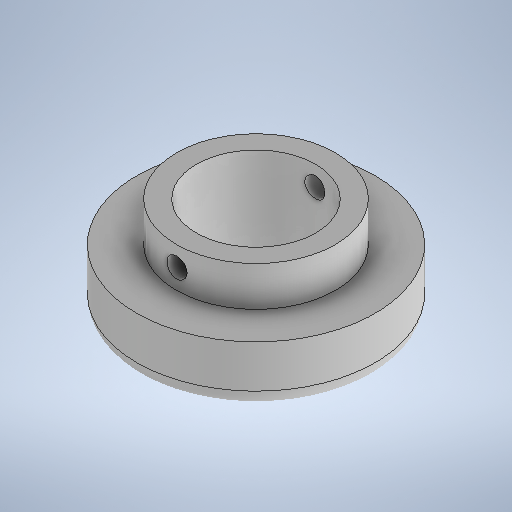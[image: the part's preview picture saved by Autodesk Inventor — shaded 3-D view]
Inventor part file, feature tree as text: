
AUTODESK INVENTOR PART (.ipt)
format: ipt  version: 2025.1 (Build 291241000, 241)  size: 282,624 bytes
history: native  units: mm
features: sketch x3, hole x2, revolve x1, fillet x1, plane x1
ambient origin geometry x8: Origin, YZ Plane, XZ Plane, XY Plane, X Axis, Y Axis, Z Axis, Center Point
bodies: Solid1 (feature_tree)
feature tree (8):
  revolve  "Revolution1"  [1 undecoded]
  hole  "Hole1"  [1 undecoded]
  fillet  "Fillet1"  [1 undecoded]
  plane  "Work Plane1"
  hole  "Hole2"  [1 undecoded]
  sketch  "Sketch1"  dims[d0=5.0mm d1=2.0mm]
  sketch  "Sketch2"  dims[d2=8.0mm d3=12.0mm d4=90.0deg]
  sketch  "Sketch3"  dims[d5=6.0mm d6=6.0mm d7=4.0mm d8=2.0mm d9=90.0deg d10=8.0mm d11=0.0mm d12=0.85mm d13=4.0mm d14=1.0mm d15=1.0mm d16=6.0mm d17=4.0mm d18=2.0mm d19=90.0deg d20=8.0mm d21=0.0mm]
note: 4 required parameter values undecoded (feature->parameter linkage not recoverable at this tier; creation-order binding heuristic only, values carry confidence <= 0.55)